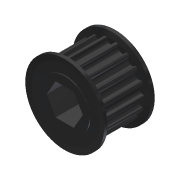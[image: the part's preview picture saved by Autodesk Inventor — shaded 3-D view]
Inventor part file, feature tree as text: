
AUTODESK INVENTOR PART (.ipt)
format: ipt  version: 2013 (Build 170138000, 138)  size: 517,120 bytes
history: native  units: in
note: dims shown in document units (in); Inventor stores cm internally (conversion verified against a paired STEP export)
features: mirror x1, other x1, imported_body x1
ambient origin geometry x8: Origin, YZ Plane, XZ Plane, XY Plane, X Axis, Y Axis, Z Axis, Center Point
feature tree (3):
  mirror  "Mirror1"
  other  "217-3226-STEP1"
  imported_body  "Base1"
